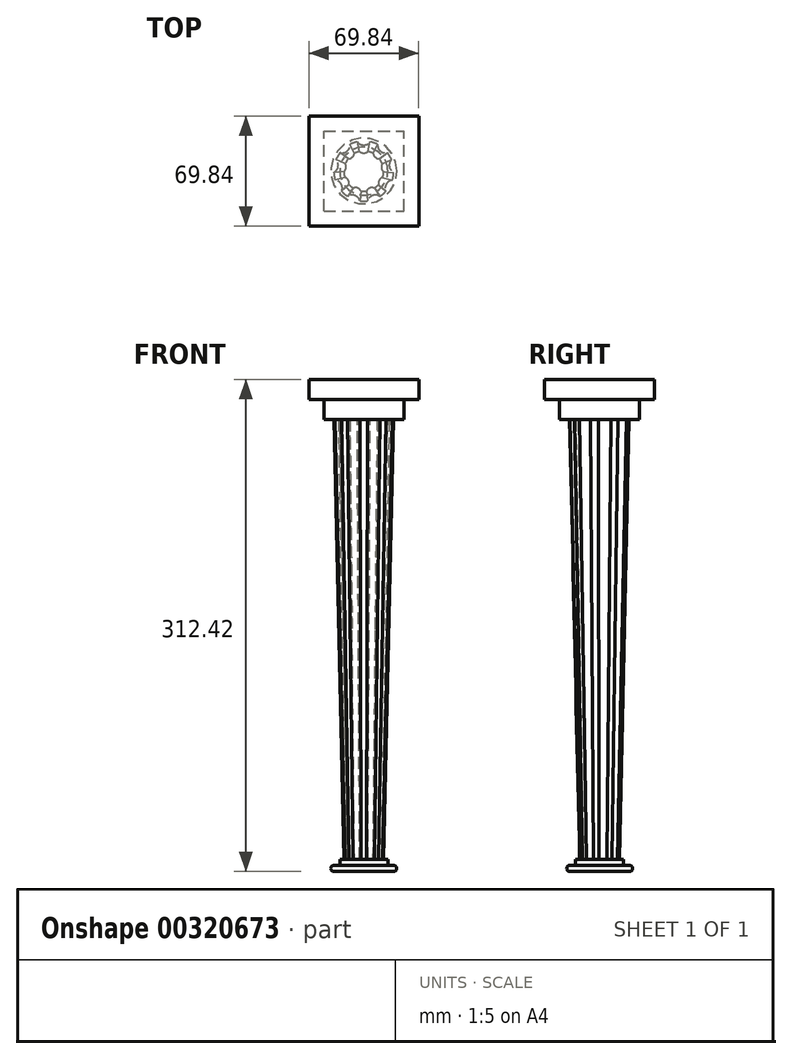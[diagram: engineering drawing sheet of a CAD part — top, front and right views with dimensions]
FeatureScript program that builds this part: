
annotation { "Feature Type Name" : "Feature", "Feature Type Description" : "" }
export const myFeature = defineFeature(function(context is Context, id is Id, definition is map)
    precondition{}
    {
        {
            var Q0;
            Q0=qCreatedBy(makeId("Top.planeOp"),FACE);
            var sketch = newSketch(context, id + "F0", { "sketchPlane" : qUnion([Q0])});
            skLineSegment(sketch, "E0.bottom", {"start": v(34.93, 34.93) * mm, "end": v(-34.93, 34.93) * mm});
            skLineSegment(sketch, "E0.top", {"start": v(34.93, -34.93) * mm, "end": v(-34.93, -34.93) * mm});
            skLineSegment(sketch, "E0.left", {"start": v(34.93, 34.93) * mm, "end": v(34.93, -34.93) * mm});
            skLineSegment(sketch, "E0.right", {"start": v(-34.93, 34.93) * mm, "end": v(-34.93, -34.93) * mm});
            skPoint(sketch, "E0.middle", {"position": v(0, 0) * mm});
            skSolve(sketch);
        }
        {
            var Q0;
            Q0=qCreatedBy(makeId("Top.planeOp"),FACE);
            var sketch = newSketch(context, id + "F1", { "sketchPlane" : qUnion([Q0])});
            skLineSegment(sketch, "E1.bottom", {"start": v(25.4, 25.4) * mm, "end": v(-25.4, 25.4) * mm});
            skLineSegment(sketch, "E1.top", {"start": v(25.4, -25.4) * mm, "end": v(-25.4, -25.4) * mm});
            skLineSegment(sketch, "E1.left", {"start": v(25.4, 25.4) * mm, "end": v(25.4, -25.4) * mm});
            skLineSegment(sketch, "E1.right", {"start": v(-25.4, 25.4) * mm, "end": v(-25.4, -25.4) * mm});
            skPoint(sketch, "E1.middle", {"position": v(0, 0) * mm});
            skSolve(sketch);
        }
        {
            var Q0;
            Q0 = qSketchRegion(id + "F1", true);
            extrude(context, id + "F2", {"entities" : qUnion([Q0]), "oppositeDirection" : true, "depth" : 25.4 * mm});
        }
        {
            var Q0;
            Q0 = qSketchRegion(id + "F0", true);
            extrude(context, id + "F3", {"entities" : qUnion([Q0]), "operationType" : NewBodyOperationType.ADD, "oppositeDirection" : true, "depth" : 12.7 * mm});
        }
        {
            var Q0;
            Q0=makeQuery(id+"F2.opExtrude","CAP_FACE",FACE,{"disambiguationData":[OSD([sQuery(id+"F1.wireOp",EDGE,"E1.bottom"),sQuery(id+"F1.wireOp",EDGE,"E1.top"),sQuery(id+"F1.wireOp",EDGE,"E1.left"),sQuery(id+"F1.wireOp",EDGE,"E1.right")])],"isStart":false});
            var sketch = newSketch(context, id + "F4", { "sketchPlane" : qUnion([Q0])});
            skArc(sketch, "E2", {"start": v(15.1, -11.6) * mm, "mid": v(16.5, -9.52) * mm, "end": v(17.6, -7.28) * mm});
            skArc(sketch, "E3", {"start": v(4.1, -18.6) * mm, "mid": v(0, -16.51) * mm, "end": v(-4.1, -18.6) * mm});
            skArc(sketch, "E4.1.0", {"start": v(15.1, -11.6) * mm, "mid": v(10.61, -12.65) * mm, "end": v(8.8, -16.9) * mm});
            skArc(sketch, "E4.2.0", {"start": v(19.03, 0.82) * mm, "mid": v(16.26, -2.87) * mm, "end": v(17.6, -7.28) * mm});
            skArc(sketch, "E4.3.0", {"start": v(14.06, 12.86) * mm, "mid": v(14.3, 8.25) * mm, "end": v(18.16, 5.74) * mm});
            skArc(sketch, "E4.4.0", {"start": v(2.5, 18.89) * mm, "mid": v(5.65, 15.51) * mm, "end": v(10.22, 16.07) * mm});
            skArc(sketch, "E4.5.0", {"start": v(-10.22, 16.07) * mm, "mid": v(-5.65, 15.51) * mm, "end": v(-2.5, 18.89) * mm});
            skArc(sketch, "E4.6.0", {"start": v(-18.16, 5.74) * mm, "mid": v(-14.3, 8.26) * mm, "end": v(-14.06, 12.86) * mm});
            skArc(sketch, "E4.7.0", {"start": v(-17.6, -7.28) * mm, "mid": v(-16.26, -2.87) * mm, "end": v(-19.03, 0.82) * mm});
            skArc(sketch, "E4.8.0", {"start": v(-8.8, -16.9) * mm, "mid": v(-10.61, -12.65) * mm, "end": v(-15.1, -11.6) * mm});
            skArc(sketch, "E5.trimOffspring", {"start": v(19.03, 0.82) * mm, "mid": v(18.76, 3.3) * mm, "end": v(18.16, 5.74) * mm});
            skArc(sketch, "E6.trimOffspring", {"start": v(14.06, 12.86) * mm, "mid": v(12.25, 14.6) * mm, "end": v(10.22, 16.07) * mm});
            skArc(sketch, "E7.trimOffspring", {"start": v(2.5, 18.89) * mm, "mid": v(0, 19.05) * mm, "end": v(-2.5, 18.89) * mm});
            skArc(sketch, "E8.trimOffspring", {"start": v(-10.22, 16.07) * mm, "mid": v(-12.25, 14.6) * mm, "end": v(-14.06, 12.86) * mm});
            skArc(sketch, "E9.trimOffspring", {"start": v(-18.16, 5.74) * mm, "mid": v(-18.76, 3.3) * mm, "end": v(-19.03, 0.82) * mm});
            skArc(sketch, "E10.trimOffspring", {"start": v(-17.6, -7.28) * mm, "mid": v(-16.5, -9.52) * mm, "end": v(-15.1, -11.6) * mm});
            skArc(sketch, "E11.trimOffspring", {"start": v(-8.8, -16.9) * mm, "mid": v(-6.52, -17.9) * mm, "end": v(-4.1, -18.6) * mm});
            skArc(sketch, "E12.trimOffspring", {"start": v(4.1, -18.6) * mm, "mid": v(6.52, -17.9) * mm, "end": v(8.8, -16.9) * mm});
            skSolve(sketch);
        }
        {
            var Q0;
            Q0=qCreatedBy(makeId("Top.planeOp"),FACE);
            cPlane(context, id + "F5", {"entities" : qUnion([Q0]), "cplaneType" : CPlaneType.OFFSET, "offset" : 304.8 * mm, "oppositeDirection" : true, "width" : 152.4 * mm, "height" : 152.4 * mm});
        }
        {
            var Q0;
            Q0=qCreatedBy(id+"F5.planeOp",FACE);
            var sketch = newSketch(context, id + "F6", { "sketchPlane" : qUnion([Q0])});
            skArc(sketch, "E13", {"start": v(6.67, -10.8) * mm, "mid": v(8.16, -9.73) * mm, "end": v(9.47, -8.46) * mm});
            skArc(sketch, "E14", {"start": v(-2.57, 12.44) * mm, "mid": v(0, 11.43) * mm, "end": v(2.59, 12.43) * mm});
            skArc(sketch, "E15.1.0", {"start": v(-9.96, 7.87) * mm, "mid": v(-7.34, 8.76) * mm, "end": v(-6.01, 11.19) * mm});
            skArc(sketch, "E15.2.0", {"start": v(-12.7, -0.37) * mm, "mid": v(-11.26, 2) * mm, "end": v(-11.8, 4.7) * mm});
            skArc(sketch, "E15.3.0", {"start": v(-9.49, -8.45) * mm, "mid": v(-9.9, -5.7) * mm, "end": v(-12.06, -3.98) * mm});
            skArc(sketch, "E15.4.0", {"start": v(-1.84, -12.57) * mm, "mid": v(-3.92, -10.74) * mm, "end": v(-6.68, -10.8) * mm});
            skArc(sketch, "E15.5.0", {"start": v(6.67, -10.8) * mm, "mid": v(3.9, -10.74) * mm, "end": v(1.82, -12.57) * mm});
            skArc(sketch, "E15.6.0", {"start": v(12.06, -4) * mm, "mid": v(9.9, -5.72) * mm, "end": v(9.47, -8.46) * mm});
            skArc(sketch, "E15.7.0", {"start": v(11.8, 4.7) * mm, "mid": v(11.26, 1.98) * mm, "end": v(12.7, -0.39) * mm});
            skArc(sketch, "E15.8.0", {"start": v(6.02, 11.18) * mm, "mid": v(7.35, 8.75) * mm, "end": v(9.97, 7.86) * mm});
            skArc(sketch, "E16.trimOffspring", {"start": v(12.06, -4) * mm, "mid": v(12.5, -2.21) * mm, "end": v(12.7, -0.39) * mm});
            skArc(sketch, "E17.trimOffspring", {"start": v(11.8, 4.7) * mm, "mid": v(11, 6.34) * mm, "end": v(9.97, 7.86) * mm});
            skArc(sketch, "E18.trimOffspring", {"start": v(6.02, 11.18) * mm, "mid": v(4.35, 11.93) * mm, "end": v(2.59, 12.43) * mm});
            skArc(sketch, "E19.trimOffspring", {"start": v(-2.57, 12.44) * mm, "mid": v(-4.34, 11.94) * mm, "end": v(-6.01, 11.19) * mm});
            skArc(sketch, "E20.trimOffspring", {"start": v(-9.96, 7.87) * mm, "mid": v(-11, 6.36) * mm, "end": v(-11.8, 4.7) * mm});
            skArc(sketch, "E21.trimOffspring", {"start": v(-12.7, -0.37) * mm, "mid": v(-12.5, -2.2) * mm, "end": v(-12.06, -3.98) * mm});
            skArc(sketch, "E22.trimOffspring", {"start": v(-9.49, -8.45) * mm, "mid": v(-8.17, -9.72) * mm, "end": v(-6.68, -10.8) * mm});
            skArc(sketch, "E23.trimOffspring", {"start": v(-1.84, -12.57) * mm, "mid": v(0, -12.7) * mm, "end": v(1.82, -12.57) * mm});
            skSolve(sketch);
        }
        {
            var Q1;
            Q1=makeQuery(id+"F6.imprint","IMPRINT",FACE,{"disambiguationData":[TD([[makeQuery(id+"F6.imprint","IMPRINT",EDGE,{"derivedFrom":sQuery(id+"F6.wireOp",EDGE,"E13")}),1.0]])]});
            var Q2;
            Q2=makeQuery(id+"F4.imprint","IMPRINT",FACE,{"disambiguationData":[TD([[makeQuery(id+"F4.imprint","IMPRINT",EDGE,{"derivedFrom":sQuery(id+"F4.wireOp",EDGE,"E2")}),1.0]])]});
            loft(context, id + "F7", {"operationType" : NewBodyOperationType.ADD, "sheetProfilesArray" : [{ "sheetProfileEntities" : qUnion([Q1]) }, { "sheetProfileEntities" : qUnion([Q2]) }]});
        }
        {
            var Q0;
            Q0=makeQuery(id+"F7.opLoft","CAP_FACE",FACE,{"disambiguationData":[OSD([makeQuery(id+"F6.imprint","IMPRINT",FACE,{"disambiguationData":[TD([[makeQuery(id+"F6.imprint","IMPRINT",EDGE,{"derivedFrom":sQuery(id+"F6.wireOp",EDGE,"E13")}),1.0]])]})])],"isStart":true});
            var sketch = newSketch(context, id + "F8", { "sketchPlane" : qUnion([Q0])});
            skLineSegment(sketch, "E24", {"start": v(0, 0) * mm, "end": v(11.35, 10.17) * mm});
            skSolve(sketch);
        }
        {
            var Q0;
            Q0=sQuery(id+"F8.wireOp",VERTEX,"E24.end");
            var Q1;
            Q1=sQuery(id+"F8.wireOp",VERTEX,"E24.start");
            var Q2;
            Q2=qCreatedBy(makeId("Origin.pointOp"),VERTEX);
            cPlane(context, id + "F9", {"entities" : qUnion([Q0, Q1, Q2]), "cplaneType" : CPlaneType.THREE_POINT, "offset" : 25.4 * mm, "width" : 152.4 * mm, "height" : 152.4 * mm});
        }
        {
            var Q0;
            Q0=qCreatedBy(id+"F9.planeOp",FACE);
            var sketch = newSketch(context, id + "F10", { "sketchPlane" : qUnion([Q0])});
            skLineSegment(sketch, "E25", {"start": v(0, -304.8) * mm, "end": v(0, -312.42) * mm});
            skLineSegment(sketch, "E26", {"start": v(0, -312.42) * mm, "end": v(19.05, -312.42) * mm});
            skLineSegment(sketch, "E27", {"start": v(0, -304.8) * mm, "end": v(15.24, -304.8) * mm});
            skLineSegment(sketch, "E28", {"start": v(15.24, -304.8) * mm, "end": v(15.24, -308.6) * mm});
            skLineSegment(sketch, "E29", {"start": v(15.24, -308.6) * mm, "end": v(19.05, -308.6) * mm});
            skArc(sketch, "E30", {"start": v(19.05, -312.42) * mm, "mid": v(20.96, -310.51) * mm, "end": v(19.05, -308.6) * mm});
            skSolve(sketch);
        }
        {
            var Q0;
            Q0=makeQuery(id+"F10.imprint","IMPRINT",FACE,{"disambiguationData":[TD([[makeQuery(id+"F10.imprint","IMPRINT",EDGE,{"derivedFrom":sQuery(id+"F10.wireOp",EDGE,"E25")}),1.0]])]});
            var Q1;
            Q1=sQuery(id+"F10.wireOp",EDGE,"E25");
            revolve(context, id + "F11", {"operationType" : NewBodyOperationType.ADD, "entities" : qUnion([Q0]), "axis" : qUnion([Q1]), "revolveType" : RevolveType.FULL});
        }
    });
